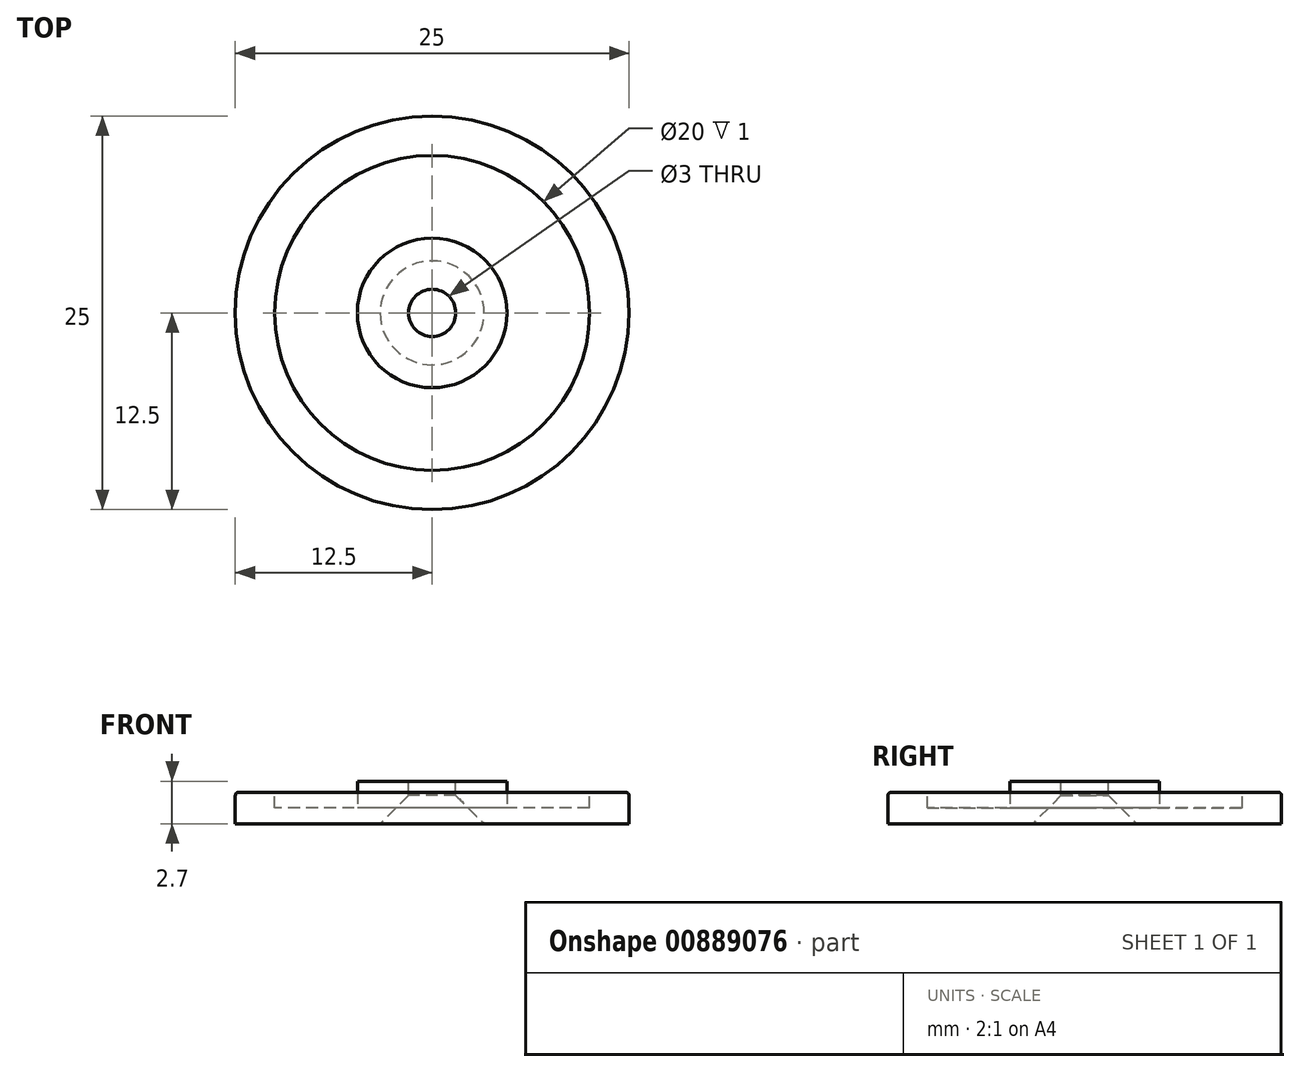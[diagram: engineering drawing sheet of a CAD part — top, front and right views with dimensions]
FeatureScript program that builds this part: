
annotation { "Feature Type Name" : "Feature", "Feature Type Description" : "" }
export const myFeature = defineFeature(function(context is Context, id is Id, definition is map)
    precondition{}
    {
        {
            var Q0;
            Q0=qCreatedBy(makeId("Top.planeOp"),FACE);
            var sketch = newSketch(context, id + "F0", { "sketchPlane" : qUnion([Q0])});
            skCircle(sketch, "E0", {"center": v(0, 0) * mm, "radius": 12.5 * mm});
            skSolve(sketch);
        }
        {
            var Q0;
            Q0=makeQuery(id+"F0.imprint","IMPRINT",FACE,{"disambiguationData":[TD([[makeQuery(id+"F0.imprint","IMPRINT",EDGE,{"derivedFrom":sQuery(id+"F0.wireOp",EDGE,"E0")}),1.0]])]});
            extrude(context, id + "F1", {"entities" : qUnion([Q0]), "depth" : 2 * mm, "offsetDistance" : 25 * mm});
        }
        {
            var Q0;
            Q0=makeQuery(id+"F1.opExtrude","CAP_FACE",FACE,{"disambiguationData":[OSD([sQuery(id+"F0.wireOp",EDGE,"E0")])],"isStart":false});
            var sketch = newSketch(context, id + "F2", { "sketchPlane" : qUnion([Q0])});
            skCircle(sketch, "E1", {"center": v(0, 0) * mm, "radius": 10 * mm});
            skSolve(sketch);
        }
        {
            var Q0;
            Q0=makeQuery(id+"F2.imprint","IMPRINT",FACE,{"disambiguationData":[TD([[makeQuery(id+"F2.imprint","IMPRINT",EDGE,{"derivedFrom":sQuery(id+"F2.wireOp",EDGE,"E1")}),1.0]])]});
            extrude(context, id + "F3", {"entities" : qUnion([Q0]), "operationType" : NewBodyOperationType.REMOVE, "oppositeDirection" : true, "depth" : 1 * mm, "offsetDistance" : 25 * mm});
        }
        {
            var Q0;
            Q0=makeQuery(id+"F3.boolean.opBoolean","COPY",FACE,{"derivedFrom":makeQuery(id+"F3.opExtrude","CAP_FACE",FACE,{"disambiguationData":[OSD([sQuery(id+"F2.wireOp",EDGE,"E1")])],"isStart":false})});
            var sketch = newSketch(context, id + "F4", { "sketchPlane" : qUnion([Q0])});
            skCircle(sketch, "E2", {"center": v(0, 0) * mm, "radius": 4.75 * mm});
            skSolve(sketch);
        }
        {
            var Q0;
            Q0=makeQuery(id+"F4.imprint","IMPRINT",FACE,{"disambiguationData":[TD([[makeQuery(id+"F4.imprint","IMPRINT",EDGE,{"derivedFrom":sQuery(id+"F4.wireOp",EDGE,"E2")}),1.0]])]});
            extrude(context, id + "F5", {"entities" : qUnion([Q0]), "operationType" : NewBodyOperationType.ADD, "depth" : 1.7 * mm, "offsetDistance" : 25 * mm});
        }
        {
            var Q0;
            Q0=makeQuery(id+"F5.opExtrude","CAP_FACE",FACE,{"disambiguationData":[OSD([sQuery(id+"F4.wireOp",EDGE,"E2")])],"isStart":false});
            var sketch = newSketch(context, id + "F6", { "sketchPlane" : qUnion([Q0])});
            skCircle(sketch, "E3", {"center": v(0, 0) * mm, "radius": 1.5 * mm});
            skSolve(sketch);
        }
        {
            var Q0;
            Q0=makeQuery(id+"F6.imprint","IMPRINT",FACE,{"disambiguationData":[TD([[makeQuery(id+"F6.imprint","IMPRINT",EDGE,{"derivedFrom":sQuery(id+"F6.wireOp",EDGE,"E3")}),1.0]])]});
            extrude(context, id + "F7", {"entities" : qUnion([Q0]), "operationType" : NewBodyOperationType.REMOVE, "oppositeDirection" : true, "depth" : 25 * mm, "offsetDistance" : 25 * mm});
        }
        {
            var Q0;
            Q0=makeQuery(id+"F7.boolean.opBoolean","INTERSECT",EDGE,{"derivedFrom":[makeQuery(id+"F1.opExtrude","CAP_FACE",FACE,{"disambiguationData":[OSD([sQuery(id+"F0.wireOp",EDGE,"E0")])],"isStart":true}),makeQuery(id+"F7.opExtrude","SWEPT_FACE",FACE,{"disambiguationData":[OSD([sQuery(id+"F6.wireOp",EDGE,"E3")])]})]});
            chamfer(context, id + "F8", {"entities" : qUnion([Q0]), "width" : 1.8 * mm, "tangentPropagation" : true});
        }
        {
            var Q0;
            Q0=makeQuery(id+"F1.opExtrude","CAP_EDGE",EDGE,{"disambiguationData":[OSD([sQuery(id+"F0.wireOp",EDGE,"E0")])],"isStart":false});
            var Q1;
            Q1=makeQuery(id+"F3.boolean.opBoolean","COPY",EDGE,{"derivedFrom":makeQuery(id+"F3.opExtrude","CAP_EDGE",EDGE,{"disambiguationData":[OSD([sQuery(id+"F2.wireOp",EDGE,"E1")])],"isStart":true})});
            fillet(context, id + "F9", {"entities" : qUnion([Q0, Q1]), "radius" : .2 * mm, "tangentPropagation" : true, "allowEdgeOverflow" : false});
        }
    });
